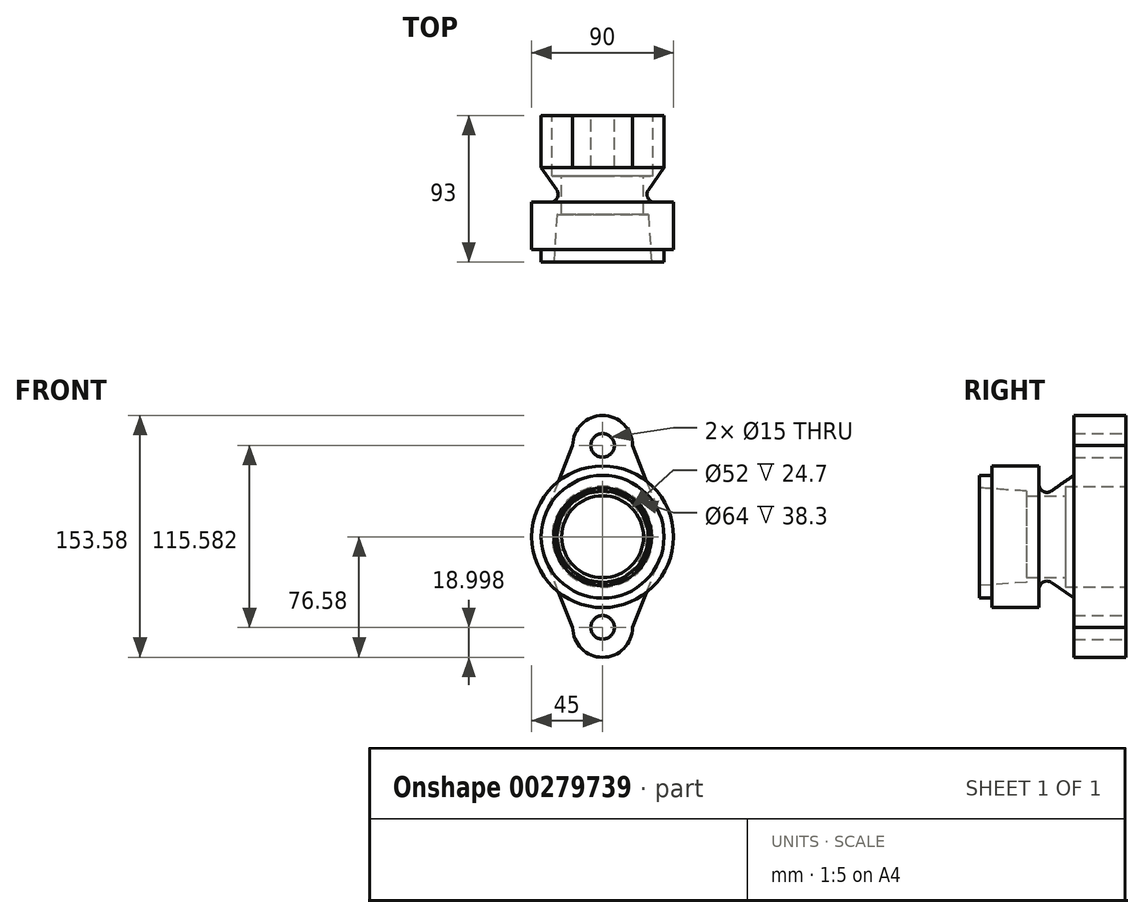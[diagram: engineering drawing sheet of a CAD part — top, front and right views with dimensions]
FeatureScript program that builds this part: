
annotation { "Feature Type Name" : "Feature", "Feature Type Description" : "" }
export const myFeature = defineFeature(function(context is Context, id is Id, definition is map)
    precondition{}
    {
        {
            var Q0;
            Q0=qCreatedBy(makeId("Right.planeOp"),FACE);
            var sketch = newSketch(context, id + "F0", { "sketchPlane" : qUnion([Q0])});
            skLineSegment(sketch, "E0", {"start": v(0, 31) * mm, "end": v(0, 39) * mm});
            skLineSegment(sketch, "E1", {"start": v(8, 45) * mm, "end": v(38, 45) * mm});
            skLineSegment(sketch, "E2", {"start": v(38, 45) * mm, "end": v(38, 33.2) * mm});
            skLineSegment(sketch, "E3", {"start": v(45.87, 29.1) * mm, "end": v(60, 39) * mm});
            skLineSegment(sketch, "E4", {"start": v(60, 39) * mm, "end": v(93, 39) * mm});
            skLineSegment(sketch, "E5", {"start": v(93, 39) * mm, "end": v(93, 32) * mm});
            skLineSegment(sketch, "E6", {"start": v(93, 32) * mm, "end": v(90, 32) * mm});
            skLineSegment(sketch, "E7", {"start": v(90, 32) * mm, "end": v(90, 0) * mm});
            skLineSegment(sketch, "E8", {"start": v(90, 0) * mm, "end": v(72, 0) * mm});
            skLineSegment(sketch, "E9", {"start": v(72, 0) * mm, "end": v(72, 26) * mm});
            skLineSegment(sketch, "E10", {"start": v(72, 26) * mm, "end": v(30, 26) * mm});
            skLineSegment(sketch, "E11", {"start": v(30, 26) * mm, "end": v(30, 29) * mm});
            skPoint(sketch, "E12.visualSharp", {"position": v(50, 32) * mm});
            skArc(sketch, "E12.filletArc", {"start": v(38, 33.2) * mm, "mid": v(40.7, 28.77) * mm, "end": v(45.87, 29.1) * mm});
            skLineSegment(sketch, "E13", {"start": v(0, 31) * mm, "end": v(30, 29) * mm});
            skLineSegment(sketch, "E14", {"start": v(0, 39) * mm, "end": v(8, 39) * mm});
            skLineSegment(sketch, "E15", {"start": v(8, 39) * mm, "end": v(8, 45) * mm});
            skSolve(sketch);
        }
        {
            var Q0;
            Q0=makeQuery(id+"F0.imprint","IMPRINT",FACE,{"disambiguationData":[TD([[makeQuery(id+"F0.imprint","IMPRINT",EDGE,{"derivedFrom":sQuery(id+"F0.wireOp",EDGE,"E0")}),-1.0]])]});
            var Q1;
            Q1=sQuery(id+"F0.wireOp",EDGE,"E8");
            revolve(context, id + "F1", {"entities" : qUnion([Q0]), "axis" : qUnion([Q1]), "revolveType" : RevolveType.FULL});
        }
        {
            var Q0;
            Q0=makeQuery(id+"F1.opRevolve","SWEPT_FACE",FACE,{"disambiguationData":[OSD([sQuery(id+"F0.wireOp",EDGE,"E5")])]});
            var sketch = newSketch(context, id + "F2", { "sketchPlane" : qUnion([Q0])});
            skArc(sketch, "E16", {"start": v(19, 58) * mm, "mid": v(0, 77) * mm, "end": v(-19, 58) * mm});
            skArc(sketch, "E17", {"start": v(7.5, 58) * mm, "mid": v(5.3, 63.3) * mm, "end": v(0, 65.5) * mm});
            skLineSegment(sketch, "E18", {"start": v(-23.6, 58) * mm, "end": v(-19, 58) * mm, "construction": true});
            skPoint(sketch, "E19.orphan", {"position": v(0, 0) * mm});
            skCircle(sketch, "E20", {"center": v(0, 0) * mm, "radius": 39 * mm});
            skLineSegment(sketch, "E21", {"start": v(-19, 58) * mm, "end": v(-36.27, 14.34) * mm});
            skLineSegment(sketch, "E22", {"start": v(19, 58) * mm, "end": v(36.27, 14.34) * mm});
            skLineSegment(sketch, "E23.MirrorCS", {"start": v(23.6, 58) * mm, "end": v(19, 58) * mm, "construction": true});
            skLineSegment(sketch, "E24.MirrorCS", {"start": v(23.6, 58) * mm, "end": v(-25.28, 58) * mm, "construction": true});
            skArc(sketch, "E25.MirrorCS", {"start": v(-19, 58) * mm, "mid": v(0, 77) * mm, "end": v(19, 58) * mm});
            skLineSegment(sketch, "E26.MirrorCS", {"start": v(-23.6, 58) * mm, "end": v(25.28, 58) * mm, "construction": true});
            skLineSegment(sketch, "E27.MirrorCS", {"start": v(-23.6, 58) * mm, "end": v(0, 58) * mm, "construction": true});
            skLineSegment(sketch, "E28.MirrorCS", {"start": v(-23.6, 58) * mm, "end": v(-7.5, 58) * mm, "construction": true});
            skLineSegment(sketch, "E29.MirrorC", {"start": v(0, 50.5) * mm, "end": v(0, 50.5) * mm});
            skCircle(sketch, "E30.MirrorC", {"center": v(0, 58) * mm, "radius": 7.5 * mm});
            skLineSegment(sketch, "E31", {"start": v(-22.86, -57.58) * mm, "end": v(-19, -57.58) * mm});
            skCircle(sketch, "E32", {"center": v(0, -57.58) * mm, "radius": 7.5 * mm});
            skArc(sketch, "E33", {"start": v(-19, -57.58) * mm, "mid": v(0, -76.58) * mm, "end": v(19, -57.58) * mm});
            skLineSegment(sketch, "E34", {"start": v(-19, -57.58) * mm, "end": v(-36.22, -14.46) * mm});
            skLineSegment(sketch, "E35", {"start": v(19, -57.58) * mm, "end": v(36.22, -14.46) * mm});
            skLineSegment(sketch, "E36.trimOffspring", {"start": v(0, 77) * mm, "end": v(0, 78.56) * mm, "construction": true});
            skLineSegment(sketch, "E37.trimOffspring", {"start": v(7.5, 58) * mm, "end": v(-25.28, 58) * mm, "construction": true});
            skLineSegment(sketch, "E38.trimOffspring", {"start": v(-19, 58) * mm, "end": v(-25.28, 58) * mm, "construction": true});
            skLineSegment(sketch, "E39.trimOffspring", {"start": v(19, -57.58) * mm, "end": v(24.77, -57.58) * mm});
            skLineSegment(sketch, "E40.trimOffspring", {"start": v(7.5, 58) * mm, "end": v(-7.5, 58) * mm, "construction": true});
            skLineSegment(sketch, "E41.trimOffspring", {"start": v(19, 58) * mm, "end": v(25.28, 58) * mm, "construction": true});
            skLineSegment(sketch, "E42.trimOffspring", {"start": v(7.5, 58) * mm, "end": v(25.28, 58) * mm, "construction": true});
            skSolve(sketch);
        }
        {
            var Q0;
            {var subQ1=sQuery(id+"F2.wireOp",EDGE,"E22");Q0=makeQuery(id+"F2.imprint","IMPRINT",FACE,{"disambiguationData":[TD([[makeQuery(id+"F2.imprint","IMPRINT",EDGE,{"derivedFrom":subQ1}),-1.0]])]});}
            var Q1;
            Q1=makeQuery(id+"F2.imprint","IMPRINT",FACE,{"disambiguationData":[TD([[makeQuery(id+"F2.imprint","IMPRINT",EDGE,{"derivedFrom":sQuery(id+"F2.wireOp",EDGE,"E32")}),-1.0]])]});
            extrude(context, id + "F3", {"entities" : qUnion([Q0, Q1]), "operationType" : NewBodyOperationType.ADD, "oppositeDirection" : true, "depth" : 33 * mm});
        }
        {
            var Q0;
            Q0=makeQuery(id+"F1.opRevolve","SWEPT_FACE",FACE,{"disambiguationData":[OSD([sQuery(id+"F0.wireOp",EDGE,"E7")])]});
            var sketch = newSketch(context, id + "F4", { "sketchPlane" : qUnion([Q0])});
            skCircle(sketch, "E43", {"center": v(0, 0) * mm, "radius": 32 * mm});
            skSolve(sketch);
        }
        {
            var Q0;
            Q0=makeQuery(id+"F4.imprint","IMPRINT",FACE,{"disambiguationData":[TD([[makeQuery(id+"F4.imprint","IMPRINT",EDGE,{"derivedFrom":sQuery(id+"F4.wireOp",EDGE,"E43")}),1.0]])]});
            extrude(context, id + "F5", {"entities" : qUnion([Q0]), "operationType" : NewBodyOperationType.REMOVE, "oppositeDirection" : true, "depth" : 35.3 * mm});
        }
    });
